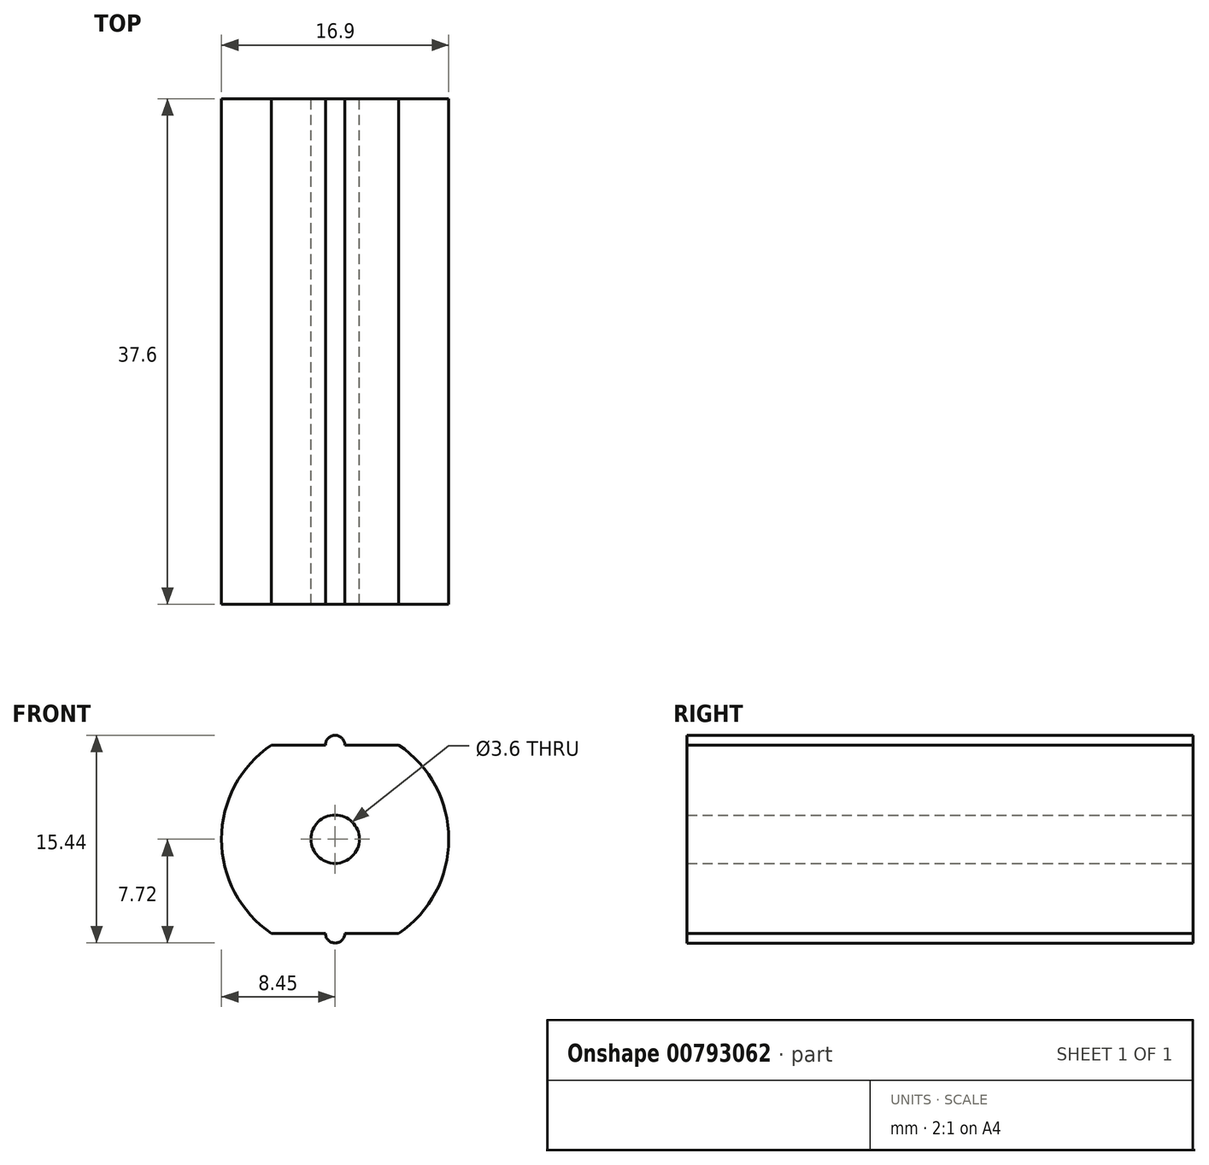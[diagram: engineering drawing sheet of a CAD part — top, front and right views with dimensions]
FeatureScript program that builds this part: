
annotation { "Feature Type Name" : "Feature", "Feature Type Description" : "" }
export const myFeature = defineFeature(function(context is Context, id is Id, definition is map)
    precondition{}
    {
        {
            var Q0;
            Q0=qCreatedBy(makeId("Front.planeOp"),FACE);
            var sketch = newSketch(context, id + "F0", { "sketchPlane" : qUnion([Q0])});
            skArc(sketch, "E0", {"start": v(-4.73, 7) * mm, "mid": v(-8.45, 0) * mm, "end": v(-4.73, -7) * mm});
            skCircle(sketch, "E1", {"center": v(0, 0) * mm, "radius": 1.13 * mm});
            skCircle(sketch, "E2", {"center": v(0, 0) * mm, "radius": 1.8 * mm});
            skArc(sketch, "E3.trimOffspring", {"start": v(4.73, -7) * mm, "mid": v(8.45, 0) * mm, "end": v(4.73, 7) * mm});
            skPoint(sketch, "E4.center.orphan", {"position": v(0, 7) * mm});
            skPoint(sketch, "E5.center.orphan", {"position": v(0, -7) * mm});
            skLineSegment(sketch, "E6", {"start": v(-4.73, 7) * mm, "end": v(-0.72, 7) * mm});
            skLineSegment(sketch, "E7", {"start": v(-4.73, -7) * mm, "end": v(-0.72, -7) * mm});
            skArc(sketch, "E8", {"start": v(0.73, 7) * mm, "mid": v(0, 7.72) * mm, "end": v(-0.72, 7) * mm});
            skArc(sketch, "E9", {"start": v(-0.72, -7) * mm, "mid": v(0, -7.72) * mm, "end": v(0.73, -7) * mm});
            skLineSegment(sketch, "E10.trimOffspring", {"start": v(0.73, 7) * mm, "end": v(4.73, 7) * mm});
            skLineSegment(sketch, "E11.trimOffspring", {"start": v(0.73, -7) * mm, "end": v(4.73, -7) * mm});
            skSolve(sketch);
        }
        {
            var Q0;
            Q0=makeQuery(id+"F0.imprint","IMPRINT",FACE,{"disambiguationData":[TD([[makeQuery(id+"F0.imprint","IMPRINT",EDGE,{"derivedFrom":sQuery(id+"F0.wireOp",EDGE,"E0")}),1.0]])]});
            extrude(context, id + "F1", {"entities" : qUnion([Q0]), "endBound" : BoundingType.SYMMETRIC, "depth" : 37.6 * mm, "offsetDistance" : 25 * mm});
        }
    });
